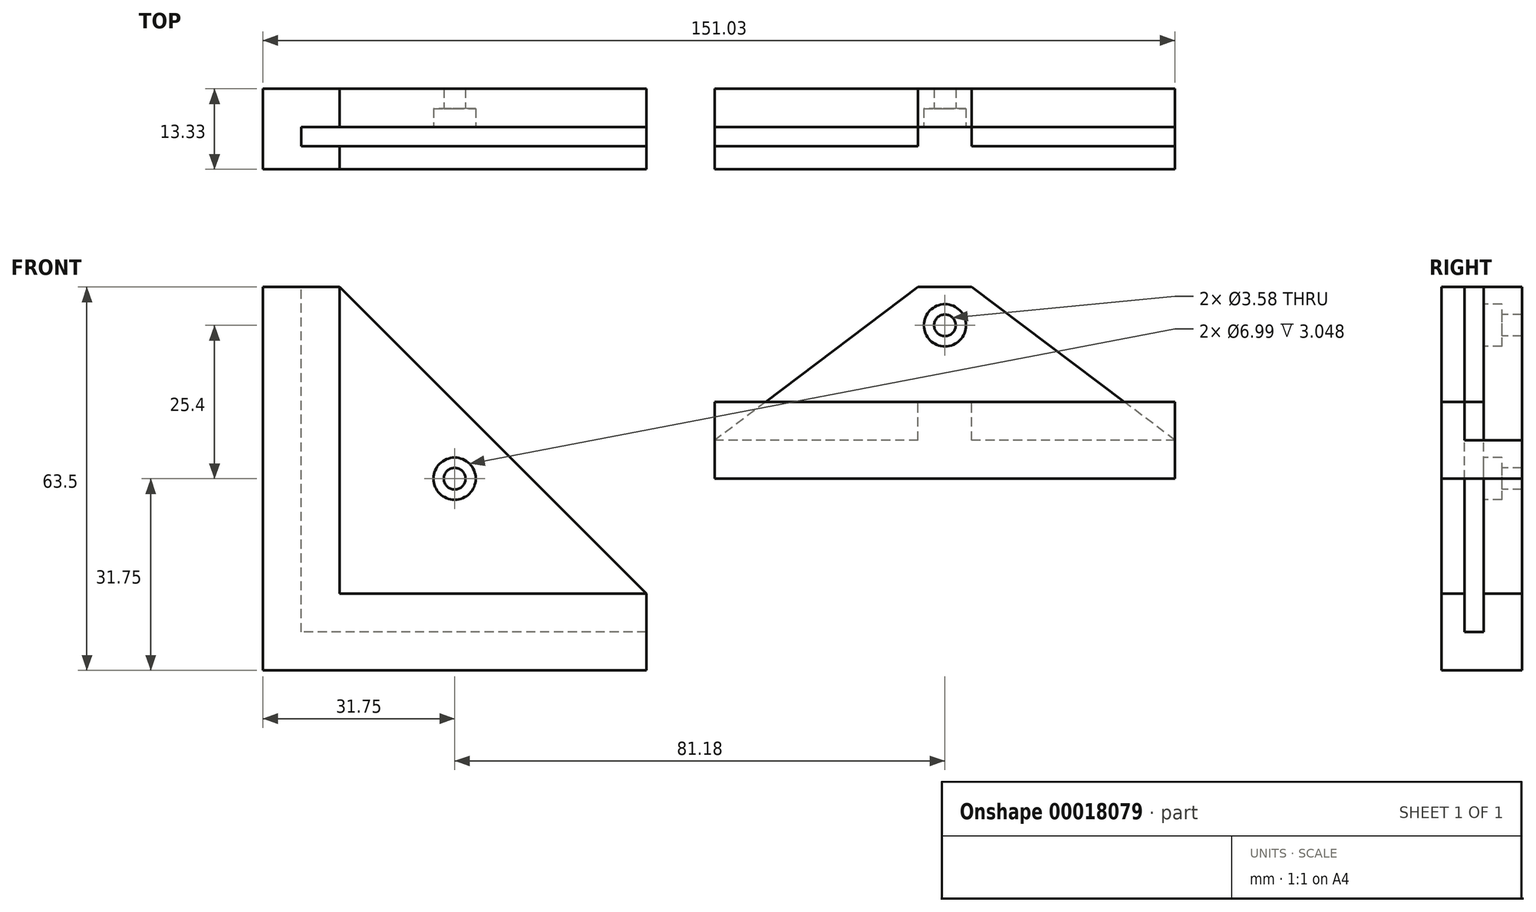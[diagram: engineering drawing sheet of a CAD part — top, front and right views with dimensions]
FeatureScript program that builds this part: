
annotation { "Feature Type Name" : "Feature", "Feature Type Description" : "" }
export const myFeature = defineFeature(function(context is Context, id is Id, definition is map)
    precondition{}
    {
        {
            var Q0;
            Q0=qCreatedBy(makeId("Front.planeOp"),FACE);
            var sketch = newSketch(context, id + "F0", { "sketchPlane" : qUnion([Q0])});
            skLineSegment(sketch, "E0.rect.bottom", {"start": v(31.75, 31.75) * mm, "end": v(-31.75, 31.75) * mm});
            skLineSegment(sketch, "E0.rect.top", {"start": v(31.75, -31.75) * mm, "end": v(-31.75, -31.75) * mm});
            skLineSegment(sketch, "E0.rect.left", {"start": v(31.75, 31.75) * mm, "end": v(31.75, -31.75) * mm});
            skLineSegment(sketch, "E0.rect.right", {"start": v(-31.75, 31.75) * mm, "end": v(-31.75, -31.75) * mm});
            skPoint(sketch, "E0.rect.middle", {"position": v(0, 0) * mm});
            skSolve(sketch);
        }
        {
            var Q0;
            Q0 = qSketchRegion(id + "F0", true);
            extrude(context, id + "F1", {"entities" : qUnion([Q0]), "depth" : 6.35 * mm});
        }
        {
            var Q0;
            Q0=makeQuery(id+"F1.opExtrude","CAP_FACE",FACE,{"disambiguationData":[OSD([sQuery(id+"F0.wireOp",EDGE,"E0.rect.bottom"),sQuery(id+"F0.wireOp",EDGE,"E0.rect.top"),sQuery(id+"F0.wireOp",EDGE,"E0.rect.left"),sQuery(id+"F0.wireOp",EDGE,"E0.rect.right")])],"isStart":false});
            var sketch = newSketch(context, id + "F2", { "sketchPlane" : qUnion([Q0])});
            skLineSegment(sketch, "E1.0.1", {"start": v(31.75, 31.75) * mm, "end": v(-31.75, 31.75) * mm});
            skLineSegment(sketch, "E1.0.2", {"start": v(-31.75, 31.75) * mm, "end": v(-31.75, -31.75) * mm});
            skLineSegment(sketch, "E1.0.3", {"start": v(-31.75, -31.75) * mm, "end": v(31.75, -31.75) * mm});
            skLineSegment(sketch, "E2", {"start": v(31.75, -31.75) * mm, "end": v(31.75, -25.4) * mm});
            skLineSegment(sketch, "E3", {"start": v(31.75, -25.4) * mm, "end": v(-25.4, -25.4) * mm});
            skLineSegment(sketch, "E4", {"start": v(-25.4, -25.4) * mm, "end": v(-25.4, 31.75) * mm});
            skSolve(sketch);
        }
        {
            var Q0;
            Q0 = qSketchRegion(id + "F2", true);
            extrude(context, id + "F3", {"entities" : qUnion([Q0]), "operationType" : NewBodyOperationType.ADD, "depth" : 3.17 * mm});
        }
        {
            var Q0;
            Q0=makeQuery(id+"F3.opExtrude","CAP_FACE",FACE,{"disambiguationData":[OSD([sQuery(id+"F2.wireOp",EDGE,"E1.0.1"),sQuery(id+"F2.wireOp",EDGE,"E1.0.2"),sQuery(id+"F2.wireOp",EDGE,"E1.0.3"),sQuery(id+"F2.wireOp",EDGE,"E2"),sQuery(id+"F2.wireOp",EDGE,"E3"),sQuery(id+"F2.wireOp",EDGE,"E4")])],"isStart":false});
            var sketch = newSketch(context, id + "F4", { "sketchPlane" : qUnion([Q0])});
            skLineSegment(sketch, "E5.0.0", {"start": v(31.75, -31.75) * mm, "end": v(31.75, -25.4) * mm});
            skLineSegment(sketch, "E5.0.3", {"start": v(-25.4, 31.75) * mm, "end": v(-31.75, 31.75) * mm});
            skLineSegment(sketch, "E5.0.4", {"start": v(-31.75, 31.75) * mm, "end": v(-31.75, -31.75) * mm});
            skLineSegment(sketch, "E5.0.5", {"start": v(-31.75, -31.75) * mm, "end": v(31.75, -31.75) * mm});
            skLineSegment(sketch, "E6", {"start": v(-25.4, 31.75) * mm, "end": v(31.75, -25.4) * mm});
            skSolve(sketch);
        }
        {
            var Q0;
            Q0 = qSketchRegion(id + "F4", true);
            extrude(context, id + "F5", {"entities" : qUnion([Q0]), "operationType" : NewBodyOperationType.ADD, "depth" : 3.8 * mm});
        }
        {
            var Q0;
            Q0=makeQuery(id+"F1.opExtrude","CAP_FACE",FACE,{"disambiguationData":[OSD([sQuery(id+"F0.wireOp",EDGE,"E0.rect.bottom"),sQuery(id+"F0.wireOp",EDGE,"E0.rect.top"),sQuery(id+"F0.wireOp",EDGE,"E0.rect.left"),sQuery(id+"F0.wireOp",EDGE,"E0.rect.right")])],"isStart":false});
            var sketch = newSketch(context, id + "F6", { "sketchPlane" : qUnion([Q0])});
            skCircle(sketch, "E7", {"center": v(0, 0) * mm, "radius": 1.8 * mm});
            skSolve(sketch);
        }
        {
            var Q0;
            Q0=qCreatedBy(makeId("Front.planeOp"),FACE);
            var sketch = newSketch(context, id + "F7", { "sketchPlane" : qUnion([Q0])});
            skLineSegment(sketch, "E8", {"start": v(43.08, 0) * mm, "end": v(119.28, 0) * mm});
            skLineSegment(sketch, "E9", {"start": v(119.28, 0) * mm, "end": v(119.28, 6.35) * mm});
            skLineSegment(sketch, "E10", {"start": v(119.28, 6.35) * mm, "end": v(85.62, 31.75) * mm});
            skLineSegment(sketch, "E11", {"start": v(85.62, 31.75) * mm, "end": v(76.73, 31.75) * mm});
            skLineSegment(sketch, "E12", {"start": v(76.73, 31.75) * mm, "end": v(43.08, 6.35) * mm});
            skLineSegment(sketch, "E13", {"start": v(43.08, 6.35) * mm, "end": v(43.08, 0) * mm});
            skSolve(sketch);
        }
        {
            var Q0;
            Q0 = qSketchRegion(id + "F7", true);
            extrude(context, id + "F8", {"entities" : qUnion([Q0]), "depth" : 6.35 * mm});
        }
        {
            var Q0;
            Q0=makeQuery(id+"F8.opExtrude","CAP_FACE",FACE,{"disambiguationData":[OSD([sQuery(id+"F7.wireOp",EDGE,"E8"),sQuery(id+"F7.wireOp",EDGE,"E9"),sQuery(id+"F7.wireOp",EDGE,"E10"),sQuery(id+"F7.wireOp",EDGE,"E11"),sQuery(id+"F7.wireOp",EDGE,"E12"),sQuery(id+"F7.wireOp",EDGE,"E13")])],"isStart":false});
            var sketch = newSketch(context, id + "F9", { "sketchPlane" : qUnion([Q0])});
            skLineSegment(sketch, "E14", {"start": v(43.08, 6.35) * mm, "end": v(43.08, 0) * mm});
            skLineSegment(sketch, "E15", {"start": v(43.08, 0) * mm, "end": v(119.28, 0) * mm});
            skLineSegment(sketch, "E16", {"start": v(119.28, 0) * mm, "end": v(119.28, 6.35) * mm});
            skLineSegment(sketch, "E17", {"start": v(119.28, 6.35) * mm, "end": v(43.08, 6.35) * mm});
            skSolve(sketch);
        }
        {
            var Q0;
            Q0 = qSketchRegion(id + "F9", true);
            extrude(context, id + "F10", {"entities" : qUnion([Q0]), "operationType" : NewBodyOperationType.ADD, "depth" : 3.17 * mm});
        }
        {
            var Q0;
            Q0=makeQuery(id+"F10.opExtrude","CAP_FACE",FACE,{"disambiguationData":[OSD([sQuery(id+"F9.wireOp",EDGE,"E14"),sQuery(id+"F9.wireOp",EDGE,"E15"),sQuery(id+"F9.wireOp",EDGE,"E16"),sQuery(id+"F9.wireOp",EDGE,"E17")])],"isStart":false});
            var sketch = newSketch(context, id + "F11", { "sketchPlane" : qUnion([Q0])});
            skLineSegment(sketch, "E18", {"start": v(43.08, 0) * mm, "end": v(43.08, 12.7) * mm});
            skLineSegment(sketch, "E19", {"start": v(43.08, 12.7) * mm, "end": v(119.28, 12.7) * mm});
            skLineSegment(sketch, "E20", {"start": v(119.28, 12.7) * mm, "end": v(119.28, 0) * mm});
            skLineSegment(sketch, "E21", {"start": v(119.28, 0) * mm, "end": v(43.08, 0) * mm});
            skSolve(sketch);
        }
        {
            var Q0;
            Q0 = qSketchRegion(id + "F11", true);
            extrude(context, id + "F12", {"entities" : qUnion([Q0]), "operationType" : NewBodyOperationType.ADD, "depth" : 3.8 * mm});
        }
        {
            var Q0;
            Q0=makeQuery(id+"F8.opExtrude","CAP_FACE",FACE,{"disambiguationData":[OSD([sQuery(id+"F7.wireOp",EDGE,"E8"),sQuery(id+"F7.wireOp",EDGE,"E9"),sQuery(id+"F7.wireOp",EDGE,"E10"),sQuery(id+"F7.wireOp",EDGE,"E11"),sQuery(id+"F7.wireOp",EDGE,"E12"),sQuery(id+"F7.wireOp",EDGE,"E13")])],"isStart":false});
            var sketch = newSketch(context, id + "F13", { "sketchPlane" : qUnion([Q0])});
            skCircle(sketch, "E22", {"center": v(81.18, 25.4) * mm, "radius": 1.8 * mm});
            skSolve(sketch);
        }
        {
            var Q0;
            Q0=makeQuery(id+"F12.opExtrude","SWEPT_FACE",FACE,{"disambiguationData":[OSD([sQuery(id+"F11.wireOp",EDGE,"E19")])]});
            var sketch = newSketch(context, id + "F14", { "sketchPlane" : qUnion([Q0])});
            skLineSegment(sketch, "E23", {"start": v(76.73, -9.53) * mm, "end": v(76.73, -6.35) * mm});
            skLineSegment(sketch, "E24", {"start": v(76.73, -6.35) * mm, "end": v(85.62, -6.35) * mm});
            skLineSegment(sketch, "E25", {"start": v(85.62, -6.35) * mm, "end": v(85.62, -9.53) * mm});
            skLineSegment(sketch, "E26", {"start": v(85.62, -9.53) * mm, "end": v(76.73, -9.53) * mm});
            skSolve(sketch);
        }
        {
            var Q0;
            Q0 = qSketchRegion(id + "F14", true);
            extrude(context, id + "F15", {"entities" : qUnion([Q0]), "operationType" : NewBodyOperationType.ADD, "oppositeDirection" : true, "depth" : 6.35 * mm});
        }
        {
            var Q0;
            Q0=makeQuery(id+"F5.opExtrude","CAP_FACE",FACE,{"disambiguationData":[OSD([sQuery(id+"F4.wireOp",EDGE,"E5.0.0"),sQuery(id+"F4.wireOp",EDGE,"E5.0.3"),sQuery(id+"F4.wireOp",EDGE,"E5.0.4"),sQuery(id+"F4.wireOp",EDGE,"E5.0.5"),sQuery(id+"F4.wireOp",EDGE,"E6")])],"isStart":false});
            var sketch = newSketch(context, id + "F16", { "sketchPlane" : qUnion([Q0])});
            skLineSegment(sketch, "E27.0.0", {"start": v(31.75, -31.75) * mm, "end": v(31.75, -25.4) * mm});
            skLineSegment(sketch, "E27.0.1", {"start": v(31.75, -25.4) * mm, "end": v(-25.4, 31.75) * mm});
            skLineSegment(sketch, "E27.0.2", {"start": v(-25.4, 31.75) * mm, "end": v(-31.75, 31.75) * mm});
            skLineSegment(sketch, "E27.0.4", {"start": v(-31.75, -31.75) * mm, "end": v(31.75, -31.75) * mm});
            skLineSegment(sketch, "E28", {"start": v(25.4, -19.05) * mm, "end": v(-19.05, -19.05) * mm});
            skLineSegment(sketch, "E29", {"start": v(-19.05, -19.05) * mm, "end": v(-19.05, 25.4) * mm});
            skSolve(sketch);
        }
        {
            var Q0;
            Q0 = qSketchRegion(id + "F16", true);
            extrude(context, id + "F17", {"entities" : qUnion([Q0]), "operationType" : NewBodyOperationType.REMOVE, "oppositeDirection" : true, "depth" : 3.8 * mm});
        }
        {
            var Q0;
            Q0=makeQuery(id+"F5.opExtrude","CAP_FACE",FACE,{"disambiguationData":[OSD([sQuery(id+"F4.wireOp",EDGE,"E5.0.0"),sQuery(id+"F4.wireOp",EDGE,"E5.0.3"),sQuery(id+"F4.wireOp",EDGE,"E5.0.4"),sQuery(id+"F4.wireOp",EDGE,"E5.0.5"),sQuery(id+"F4.wireOp",EDGE,"E6")])],"isStart":false});
            var sketch = newSketch(context, id + "F18", { "sketchPlane" : qUnion([Q0])});
            skLineSegment(sketch, "E30", {"start": v(25.4, -19.05) * mm, "end": v(31.75, -19.05) * mm});
            skLineSegment(sketch, "E31", {"start": v(31.75, -19.05) * mm, "end": v(31.75, -25.4) * mm});
            skLineSegment(sketch, "E32", {"start": v(31.75, -25.4) * mm, "end": v(25.4, -19.05) * mm});
            skLineSegment(sketch, "E33", {"start": v(-19.05, 25.4) * mm, "end": v(-19.05, 31.75) * mm});
            skLineSegment(sketch, "E34", {"start": v(-19.05, 31.75) * mm, "end": v(-25.4, 31.75) * mm});
            skLineSegment(sketch, "E35", {"start": v(-25.4, 31.75) * mm, "end": v(-19.05, 25.4) * mm});
            skSolve(sketch);
        }
        {
            var Q0;
            Q0 = qSketchRegion(id + "F18", true);
            extrude(context, id + "F19", {"entities" : qUnion([Q0]), "operationType" : NewBodyOperationType.ADD, "oppositeDirection" : true, "depth" : 3.8 * mm});
        }
        {
            var Q0;
            Q0=qCreatedBy(makeId("Front.planeOp"),FACE);
            var sketch = newSketch(context, id + "F20", { "sketchPlane" : qUnion([Q0])});
            skLineSegment(sketch, "E36.0.0", {"start": v(31.75, -31.75) * mm, "end": v(31.75, -19.05) * mm});
            skLineSegment(sketch, "E36.0.1", {"start": v(31.75, -19.05) * mm, "end": v(-19.05, -19.05) * mm});
            skLineSegment(sketch, "E36.0.3", {"start": v(-19.05, 31.75) * mm, "end": v(-31.75, 31.75) * mm});
            skLineSegment(sketch, "E36.0.5", {"start": v(-31.75, -31.75) * mm, "end": v(31.75, -31.75) * mm});
            skLineSegment(sketch, "E37.0.1", {"start": v(-25.4, -25.4) * mm, "end": v(31.75, -25.4) * mm});
            skLineSegment(sketch, "E37.0.2", {"start": v(31.75, -25.4) * mm, "end": v(31.75, 31.75) * mm});
            skLineSegment(sketch, "E38", {"start": v(31.75, -19.05) * mm, "end": v(-19.05, 31.75) * mm});
            skLineSegment(sketch, "E39", {"start": v(-19.05, 31.75) * mm, "end": v(31.75, 31.75) * mm});
            skSolve(sketch);
        }
        {
            var Q0;
            Q0 = qSketchRegion(id + "F20", true);
            extrude(context, id + "F21", {"entities" : qUnion([Q0]), "operationType" : NewBodyOperationType.REMOVE, "depth" : 25.4 * mm});
        }
        {
            var Q0;
            Q0=sQuery(id+"F13.wireOp",VERTEX,"E22.center");
            var Q1;
            Q1=makeQuery(id+"F8.opExtrude","SWEPT_BODY",BODY,{"disambiguationData":[OSD([sQuery(id+"F7.wireOp",EDGE,"E8"),sQuery(id+"F7.wireOp",EDGE,"E9"),sQuery(id+"F7.wireOp",EDGE,"E10"),sQuery(id+"F7.wireOp",EDGE,"E11"),sQuery(id+"F7.wireOp",EDGE,"E12"),sQuery(id+"F7.wireOp",EDGE,"E13")])]});
            hole(context, id + "F22", {"style" : HoleStyle.C_BORE, "holeDiameter" : 3.58 * mm, "cBoreDiameter" : 7 * mm, "cBoreDepth" : 3.05 * mm, "endStyle" : HoleEndStyle.THROUGH, "locations" : qUnion([Q0]), "scope" : qUnion([Q1])});
        }
        {
            var Q0;
            Q0=sQuery(id+"F6.wireOp",VERTEX,"E7.center");
            var Q1;
            Q1=makeQuery(id+"F1.opExtrude","SWEPT_BODY",BODY,{"disambiguationData":[OSD([sQuery(id+"F0.wireOp",EDGE,"E0.rect.bottom"),sQuery(id+"F0.wireOp",EDGE,"E0.rect.top"),sQuery(id+"F0.wireOp",EDGE,"E0.rect.left"),sQuery(id+"F0.wireOp",EDGE,"E0.rect.right")])]});
            hole(context, id + "F23", {"style" : HoleStyle.C_BORE, "holeDiameter" : 3.58 * mm, "cBoreDiameter" : 7 * mm, "cBoreDepth" : 3.05 * mm, "endStyle" : HoleEndStyle.THROUGH, "locations" : qUnion([Q0]), "scope" : qUnion([Q1])});
        }
    });
